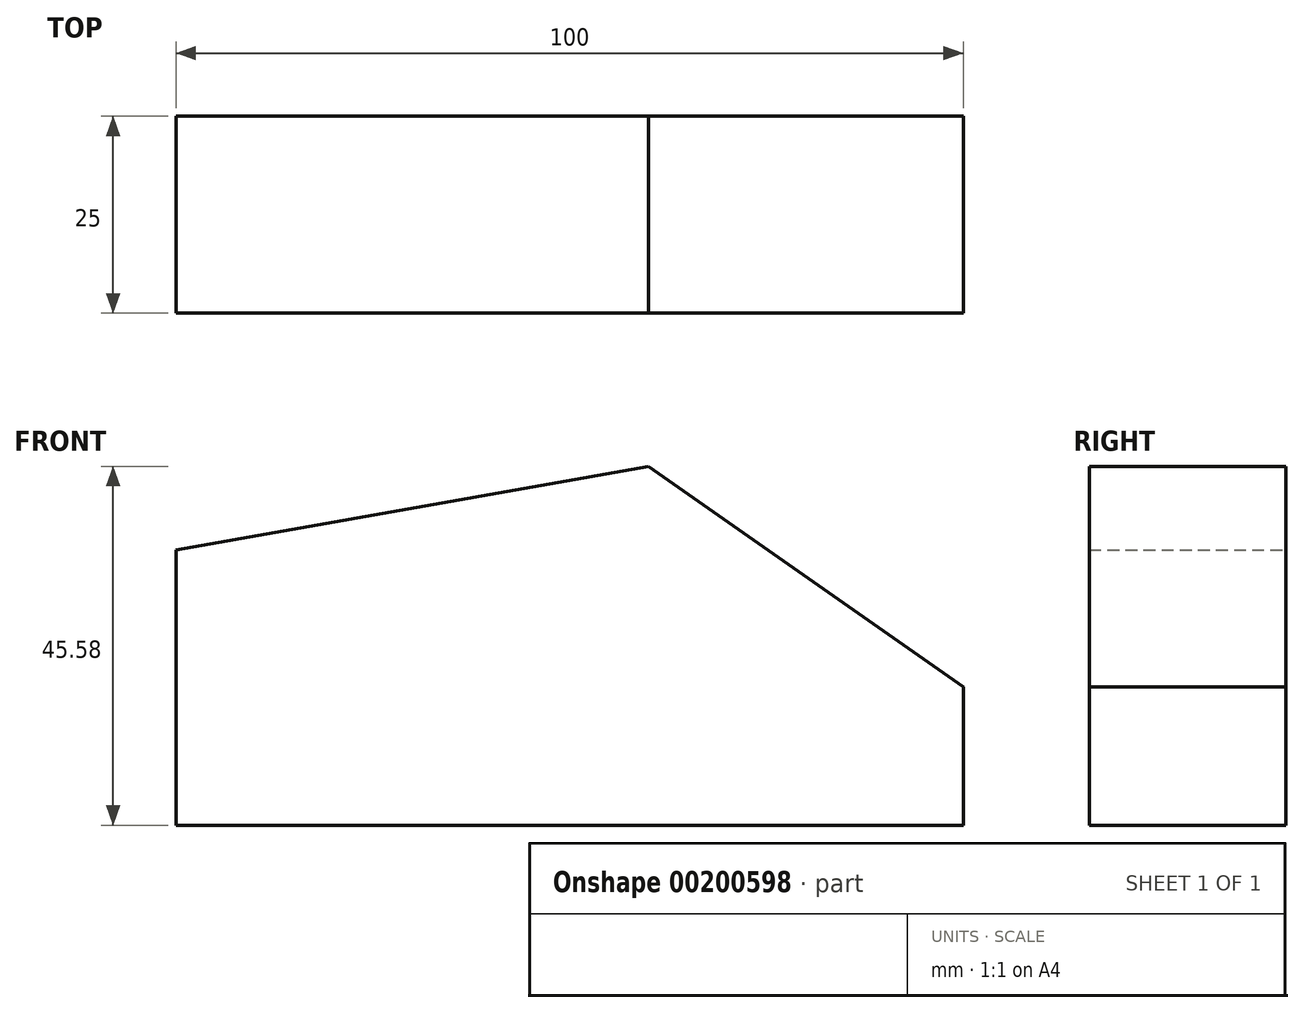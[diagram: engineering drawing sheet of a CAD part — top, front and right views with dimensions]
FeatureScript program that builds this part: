
annotation { "Feature Type Name" : "Feature", "Feature Type Description" : "" }
export const myFeature = defineFeature(function(context is Context, id is Id, definition is map)
    precondition{}
    {
        {
            var Q0;
            Q0=qCreatedBy(makeId("Front.planeOp"),FACE);
            var sketch = newSketch(context, id + "F0", { "sketchPlane" : qUnion([Q0])});
            skLineSegment(sketch, "E0", {"start": v(0, 0) * mm, "end": v(0, 17.57) * mm});
            skLineSegment(sketch, "E1", {"start": v(0, 17.57) * mm, "end": v(-40, 45.58) * mm});
            skLineSegment(sketch, "E2", {"start": v(-40, 45.58) * mm, "end": v(-100, 35) * mm});
            skLineSegment(sketch, "E3", {"start": v(-100, 35) * mm, "end": v(-100, 0) * mm});
            skLineSegment(sketch, "E4", {"start": v(-100, 0) * mm, "end": v(0, 0) * mm});
            skSolve(sketch);
        }
        {
            var Q0;
            Q0 = qSketchRegion(id + "F0", true);
            extrude(context, id + "F1", {"entities" : qUnion([Q0]), "depth" : 25 * mm});
        }
    });
